SOLIDWORKS PART (.sldprt)
format: sldprt  version: not decoded by parser v0  size: 254,464 bytes
history: native  units: mm
features: sketch x3, extrude x2, material x1, chamfer x1, fillet x1, cut_extrude x1 (+13 scaffold rows collapsed)
feature tree (22):
  scaffold x13  (default folders/planes/origin — collapsed)
  material  "Material <not specified>"
  sketch  "Sketch1"  dims[c1.D1=15.0mm c1.D2=30.0mm c1.D3=30.0mm c2.D2=26.0mm c2.D3=26.0mm]
  extrude  "Boss-Extrude1"  Depth=15mm
  chamfer  "Chamfer1"  Distance=5mm Angle=60deg
  sketch  "Sketch2"  dims[c1.D1=1.0mm c1.D2=8.0mm c2.D1=2.0mm c2.D2=8.0mm c2.D3=2.0mm c2.D4=8.0mm c3.D3=8.0mm]
  extrude  "Boss-Extrude2"  Depth=8mm
  fillet  "Fillet1"  Radius=4mm
  sketch  "Sketch5"  dims[D1=3.1mm D2=3.1mm]
  cut_extrude  "Cut-Extrude2"  [1 undecoded]
decode coverage: 7 of 8 modeling features carry decoded parameters
note: 1 parameter value undecoded
note: suppression state not decoded; provenance and decode notes live in map.json
